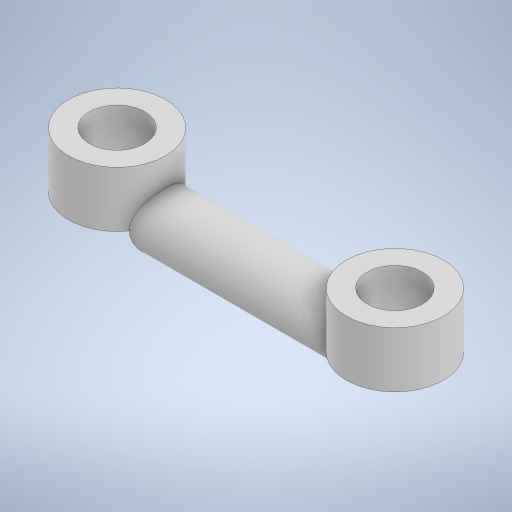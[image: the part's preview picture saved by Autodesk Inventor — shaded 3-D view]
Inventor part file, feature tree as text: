
AUTODESK INVENTOR PART (.ipt)
format: ipt  version: 2024 (Build 280153000, 153)  size: 276,480 bytes
history: native  units: in
note: dims shown in document units (in); Inventor stores cm internally (conversion verified against a paired STEP export)
features: extrude x5, sketch x3, revolve x1, mirror x1
ambient origin geometry x8: Origin, YZ Plane, XZ Plane, XY Plane, X Axis, Y Axis, Z Axis, Center Point
bodies: Solid1 (feature_tree)
feature tree (10):
  revolve  "Revolution1"  [1 undecoded]
  sketch  "Sketch2"  dims[d2=90.0deg d3=1.378in]
  extrude  "Extrusion1"  Depth=1.378in
  extrude  "Extrusion2"  Depth=0.7874in TaperAngle=0.0deg
  extrude  "Extrusion3"  Depth=0.7874in TaperAngle=0.0deg
  mirror  "Mirror1"
  sketch  "Sketch3"  dims[d4=0.7874in d5=0.7874in d6=0.0in d7=0.7874in d8=0.0in d9=0.7874in d10=0.0in d11=1.378in d12=0.7874in d13=0.7874in d14=0.0in d15=0.7874in d16=0.0in]
  extrude  "Extrusion4"  Depth=0.7874in TaperAngle=0.0deg
  extrude  "Extrusion5"  Depth=1.378in
  sketch  "Sketch1"  dims[d0=3.937in d1=0.3937in]
note: 1 required parameter value undecoded (feature->parameter linkage not recoverable at this tier; creation-order binding heuristic only, values carry confidence <= 0.55)
